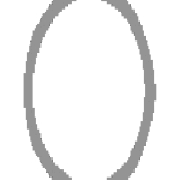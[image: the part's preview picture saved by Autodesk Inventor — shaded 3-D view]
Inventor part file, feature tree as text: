
AUTODESK INVENTOR PART (.ipt)
format: ipt  version: 2021 (Build 250183000, 183)  size: 109,568 bytes
history: native  units: in
note: dims shown in document units (in); Inventor stores cm internally (conversion verified against a paired STEP export)
features: other x4, sketch x3, plane x1
ambient origin geometry x8: Origin, YZ Plane, XZ Plane, XY Plane, X Axis, Y Axis, Z Axis, Center Point
bodies: Solid1 (feature_tree), Body (feature_tree)
feature tree (8):
  other  "Driven Length"
  other  "Frame Generator"
  other  "Start Plane"
  other  "End Plane"
  sketch  "Sketch"  dims[d2=16.9706in d4=-0.0in d5=16.9706in d6=0.12in d7=0.0in d8=90.0deg d9=16.9706in]
  sketch  "Sketch2"  dims[d0=1.0in]
  plane  "Work Plane3"
  sketch  "Sketch3"  dims[d1=0.065in]
